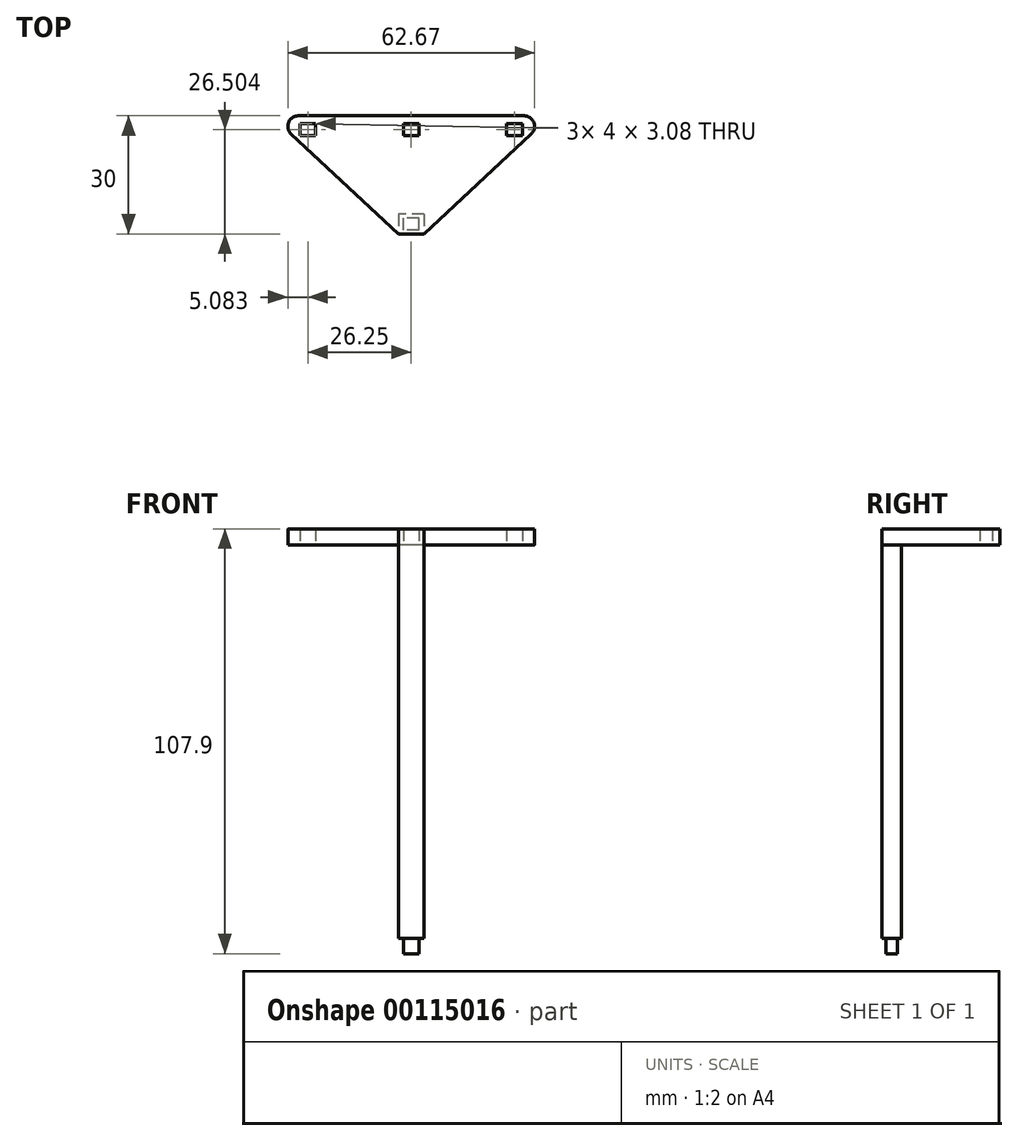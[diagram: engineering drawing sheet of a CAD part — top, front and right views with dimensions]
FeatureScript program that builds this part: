
annotation { "Feature Type Name" : "Feature", "Feature Type Description" : "" }
export const myFeature = defineFeature(function(context is Context, id is Id, definition is map)
    precondition{}
    {
        {
            var Q0;
            Q0=qCreatedBy(makeId("Top.planeOp"),FACE);
            var sketch = newSketch(context, id + "F0", { "sketchPlane" : qUnion([Q0])});
            skLineSegment(sketch, "E0.bottom", {"start": v(-25.26, -27.65) * mm, "end": v(-31.76, -27.65) * mm});
            skLineSegment(sketch, "E0.top", {"start": v(-25.26, -32.65) * mm, "end": v(-31.76, -32.65) * mm});
            skLineSegment(sketch, "E0.left", {"start": v(-25.26, -27.65) * mm, "end": v(-25.26, -32.65) * mm});
            skLineSegment(sketch, "E0.right", {"start": v(-31.76, -27.65) * mm, "end": v(-31.76, -32.65) * mm});
            skPoint(sketch, "E0.middle", {"position": v(-28.5, -30.15) * mm});
            skLineSegment(sketch, "E1.bottom", {"start": v(-26.53, -31.65) * mm, "end": v(-30.48, -31.65) * mm});
            skLineSegment(sketch, "E1.top", {"start": v(-26.53, -28.65) * mm, "end": v(-30.48, -28.65) * mm});
            skLineSegment(sketch, "E1.left", {"start": v(-26.53, -31.65) * mm, "end": v(-26.53, -28.65) * mm});
            skLineSegment(sketch, "E1.right", {"start": v(-30.48, -31.65) * mm, "end": v(-30.48, -28.65) * mm});
            skSolve(sketch);
        }
        {
            var Q0;
            Q0=makeQuery(id+"F0.imprint","IMPRINT",FACE,{"disambiguationData":[TD([[makeQuery(id+"F0.imprint","IMPRINT",EDGE,{"derivedFrom":sQuery(id+"F0.wireOp",EDGE,"E1.bottom")}),-1.0]])]});
            extrude(context, id + "F1", {"entities" : qUnion([Q0]), "oppositeDirection" : true, "depth" : 3.9 * mm});
        }
        {
            var Q0;
            Q0=makeQuery(id+"F0.imprint","IMPRINT",FACE,{"disambiguationData":[TD([[makeQuery(id+"F0.imprint","IMPRINT",EDGE,{"derivedFrom":sQuery(id+"F0.wireOp",EDGE,"E1.bottom")}),-1.0]])]});
            var Q1;
            Q1=makeQuery(id+"F0.imprint","IMPRINT",FACE,{"disambiguationData":[TD([[makeQuery(id+"F0.imprint","IMPRINT",EDGE,{"derivedFrom":sQuery(id+"F0.wireOp",EDGE,"E0.bottom")}),1.0]])]});
            extrude(context, id + "F2", {"entities" : qUnion([Q0, Q1]), "operationType" : NewBodyOperationType.ADD, "depth" : 100 * mm});
        }
        {
            var Q0;
            Q0=makeQuery(id+"F2.opExtrude","CAP_FACE",FACE,{"disambiguationData":[OSD([sQuery(id+"F0.wireOp",EDGE,"E0.bottom"),sQuery(id+"F0.wireOp",EDGE,"E0.top"),sQuery(id+"F0.wireOp",EDGE,"E0.left"),sQuery(id+"F0.wireOp",EDGE,"E0.right")])],"isStart":false});
            var sketch = newSketch(context, id + "F3", { "sketchPlane" : qUnion([Q0])});
            skLineSegment(sketch, "E2", {"start": v(-31.76, -32.65) * mm, "end": v(-64, -2.65) * mm});
            skLineSegment(sketch, "E3", {"start": v(-28.5, -32.65) * mm, "end": v(-28.5, -2.65) * mm});
            skLineSegment(sketch, "E4", {"start": v(-28.5, -2.65) * mm, "end": v(-64, -2.65) * mm});
            skLineSegment(sketch, "E5", {"start": v(-31.76, -32.65) * mm, "end": v(-28.5, -32.65) * mm});
            skLineSegment(sketch, "E6", {"start": v(-28.5, -2.65) * mm, "end": v(7, -2.65) * mm});
            skLineSegment(sketch, "E7", {"start": v(7, -2.65) * mm, "end": v(-25.26, -32.65) * mm});
            skLineSegment(sketch, "E8", {"start": v(-25.26, -32.65) * mm, "end": v(-28.5, -32.65) * mm});
            skLineSegment(sketch, "E9", {"start": v(-28.5, -2.65) * mm, "end": v(-28.5, -6.15) * mm, "construction": true});
            skLineSegment(sketch, "E10.bottom", {"start": v(-26.5, -7.68) * mm, "end": v(-30.5, -7.68) * mm});
            skLineSegment(sketch, "E10.top", {"start": v(-26.5, -4.6) * mm, "end": v(-30.5, -4.6) * mm});
            skLineSegment(sketch, "E10.left", {"start": v(-26.5, -7.68) * mm, "end": v(-26.5, -4.6) * mm});
            skLineSegment(sketch, "E10.right", {"start": v(-30.5, -7.68) * mm, "end": v(-30.5, -4.6) * mm});
            skPoint(sketch, "E10.middle", {"position": v(-28.5, -6.15) * mm});
            skLineSegment(sketch, "E11", {"start": v(-28.5, -6.15) * mm, "end": v(-54.76, -6.15) * mm, "construction": true});
            skPoint(sketch, "E11.endSnap0", {"position": v(-26.5, -6.15) * mm});
            skLineSegment(sketch, "E12.bottom", {"start": v(-52.76, -7.68) * mm, "end": v(-56.76, -7.68) * mm});
            skLineSegment(sketch, "E12.top", {"start": v(-52.76, -4.6) * mm, "end": v(-56.76, -4.6) * mm});
            skLineSegment(sketch, "E12.left", {"start": v(-52.76, -7.68) * mm, "end": v(-52.76, -4.6) * mm});
            skLineSegment(sketch, "E12.right", {"start": v(-56.76, -7.68) * mm, "end": v(-56.76, -4.6) * mm});
            skPoint(sketch, "E12.middle", {"position": v(-54.76, -6.15) * mm});
            skLineSegment(sketch, "E13", {"start": v(-28.5, -6.15) * mm, "end": v(-2.26, -6.15) * mm, "construction": true});
            skLineSegment(sketch, "E14.bottom", {"start": v(-0.26, -7.68) * mm, "end": v(-4.26, -7.68) * mm});
            skLineSegment(sketch, "E14.top", {"start": v(-0.26, -4.6) * mm, "end": v(-4.26, -4.6) * mm});
            skLineSegment(sketch, "E14.left", {"start": v(-0.26, -7.68) * mm, "end": v(-0.26, -4.6) * mm});
            skLineSegment(sketch, "E14.right", {"start": v(-4.26, -7.68) * mm, "end": v(-4.26, -4.6) * mm});
            skPoint(sketch, "E14.middle", {"position": v(-2.26, -6.15) * mm});
            skSolve(sketch);
        }
        {
            var Q0;
            Q0=makeQuery(id+"F3.imprint","IMPRINT",FACE,{"disambiguationData":[TD([[makeQuery(id+"F3.imprint","IMPRINT",EDGE,{"derivedFrom":sQuery(id+"F3.wireOp",EDGE,"E2")}),-1.0]])]});
            var Q1;
            {var subQ5=sQuery(id+"F3.wireOp",EDGE,"E6");Q1=makeQuery(id+"F3.imprint","IMPRINT",FACE,{"disambiguationData":[TD([[makeQuery(id+"F3.imprint","IMPRINT",EDGE,{"derivedFrom":subQ5}),-1.0]])]});}
            var Q2;
            {var subQ0=sQuery(id+"F3.wireOp",EDGE,"E8");Q2=makeQuery(id+"F3.imprint","IMPRINT",FACE,{"disambiguationData":[TD([[makeQuery(id+"F3.imprint","IMPRINT",EDGE,{"derivedFrom":subQ0}),-1.0]])]});}
            var Q3;
            {var subQ0=sQuery(id+"F3.wireOp",EDGE,"E5");Q3=makeQuery(id+"F3.imprint","IMPRINT",FACE,{"disambiguationData":[TD([[makeQuery(id+"F3.imprint","IMPRINT",EDGE,{"derivedFrom":subQ0}),-1.0]])]});}
            extrude(context, id + "F4", {"entities" : qUnion([Q0, Q1, Q2, Q3]), "operationType" : NewBodyOperationType.ADD, "depth" : 4 * mm});
        }
        {
            var Q0;
            Q0=makeQuery(id+"F4.opExtrude","SWEPT_EDGE",EDGE,{"disambiguationData":[OSD([sQuery(id+"F3.wireOp",EDGE,"E2"),sQuery(id+"F3.wireOp",EDGE,"E4")])]});
            var Q1;
            Q1=makeQuery(id+"F4.opExtrude","SWEPT_EDGE",EDGE,{"disambiguationData":[OSD([sQuery(id+"F3.wireOp",EDGE,"E6"),sQuery(id+"F3.wireOp",EDGE,"E7")])]});
            fillet(context, id + "F5", {"entities" : qUnion([Q0, Q1]), "radius" : 2.7 * mm, "tangentPropagation" : true, "allowEdgeOverflow" : false});
        }
    });
